# Revit family: Card_Reader-Vicon-VAX-Proximity_Reader-500R
name_source: partatom
category: Security Devices
revit_build: Autodesk Revit 2014 (Build: 20140709_2115(x64)
units: mm (PartAtom-declared; Revit-internal decimal feet)

## types (1)
- VAX-500R
    Apparent Load = 35 VA
    Assembly Code = E1010110
    Connector Description = Connector for Electrical Power
    Default Elevation = 4' - 0"
    Description = Proximity Reader with up to 8 inches read range
    Housing Material = Metal - Vicon - Cast Aluminum - Black
    Load Classification = Power
    Manufacturer = Vicon Industries
    Model = VAX-500R
    Number of Poles = 1
    Operating Temperature = -40 to 149 Degrees Fahrenheit
    Power Factor = 1
    Product Documentation Link = http://www.vicon-security.com
    Product Page URL = http://www.vicon-security.com
    URL = http://www.vicon-security.com
    Voltage = 12 V
    Voltage Range = +5 - 16 VDC
    Weight = 0.25 lb

## geometry (parser evidence)
native form markers: Sweep x6
no freeform markers — native parametric forms only
